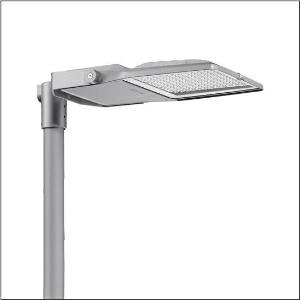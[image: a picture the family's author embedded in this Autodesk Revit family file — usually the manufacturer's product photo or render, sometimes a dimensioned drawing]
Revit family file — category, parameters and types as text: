
# Revit family: floodlight_fl_21_iq_midi___pl61_5xa7781e4c3a_96c8
name_source: partatom
category: Lighting Fixtures
units: mm (PartAtom-declared; Revit-internal decimal feet)

## family parameters
Cut with Voids When Loaded = No
Host = Face
Light Source = No
Part Type = Normal
Room Calculation Point = No
Round Connector Dimension = Use Diameter
Shared = No

## types (1)
- --- (1 x LED, 27490 lm, 208.1 W, 4000K)
    Apparent Load = 208 VA
    CIE Flux Codes = 33 65 98 100 100
    Color Rendering = 70
    Color Temperature = 4000K
    Default Elevation = 1800 mm
    Description = Floodlight FL 21 iQ midi, floodlight, primary light control with lens, of PMMA, primary optical cover: protective disc, of toughened safety glass, transparent, light distribution: PL61, light emission: direct distribution, installation type: surface-mounted, LED, High Power LED, rated luminous flux: 27.490lm, luminous efficacy: 132lm/W, light colour: 740, colour temperature: 4000K, control gear: ECG iQ, control: optimised constant luminous flux control (CLO 2.0), Desk-Remote (wireless, voltage-free reading and setting of iQ features in the workshop via application-optimized NFC function/RFID function), Light-Fading, Smart-Wire, Night-Set, Lumen-Switch, Temp-Guard, Auto-Match, with terminal, 6-pole, mains connection: 220..240V, AC, 50/60Hz, start of lifetime: 208W, end of service life: 227W, reduction: 90W, luminaire housing, of diecast aluminium, powder-coated, Siteco® metallic grey (DB 702S), corrosivity category C5 mid according to DIN EN ISO 12944, sealing non-destructively replaceable, please order mast flange separately, mast bracket, of steel, galvanised, powder-coated, Siteco® metallic grey (DB 702S), protection rating (complete): IP66, insulation class (complete): insulation class II (safety insulation), certification: CE, protection symbol: D, impact resistance: IK08, permissible operating ambient temperature: -40..+40°C, permissible operating ambient temperature for outdoor applications: -40..+50°C, standard: DIN EN 12944, LABS conformity tested according to VDMA 24364:2018-05, packaging unit: 1 piece

Light Distribution: PL61
    Height = 76 mm
    Lamp = 1 x LED
    Lamp Light Flux = 27490 lm
    Lamp Power = 208.1 W
    Lamp count = 1
    Length = 657 mm
    Luminous efficacy = 132 lm/W
    Manufacturer = Siteco
    ModVariant = No
    Model = 5XA7781E4C3A
    Number of Poles = 1
    OnlyDefault = Yes
    Power Factor = 1
    Product Name = Floodlight FL 21 iQ midi | PL61
    Product group = floodlight | pylon annexe
    ProductGroupID = 6200
    Protection Class = Protection class II
    Protection Degree = IP 66
    RLX_Detail_Level = 1
    RLX_Emergency_Light_Flux = 0 lm
    RLX_Emergency_Type = 0
    RLX_Emergency_Type_DB = No
    RlxData = <blob elided: 153713 chars, md5=79256d55>
    Socket = socket
    Standby Power = 0 W
    System Light Flux = 27490 lm
    System Power = 208 W
    Type Comments = factory setting: luminous flux: 100 % | dim-lin: 254 | 710 mA
    Type Image = l_1007123.jpg
    URL = http://relux.com
    VarID = @adj_038989
    Voltage = 0 V
    Weight = 0.00 kg
    Width = 442 mm

## geometry (parser evidence)
native form markers: Blend x4, Sweep x15
no freeform markers — native parametric forms only
